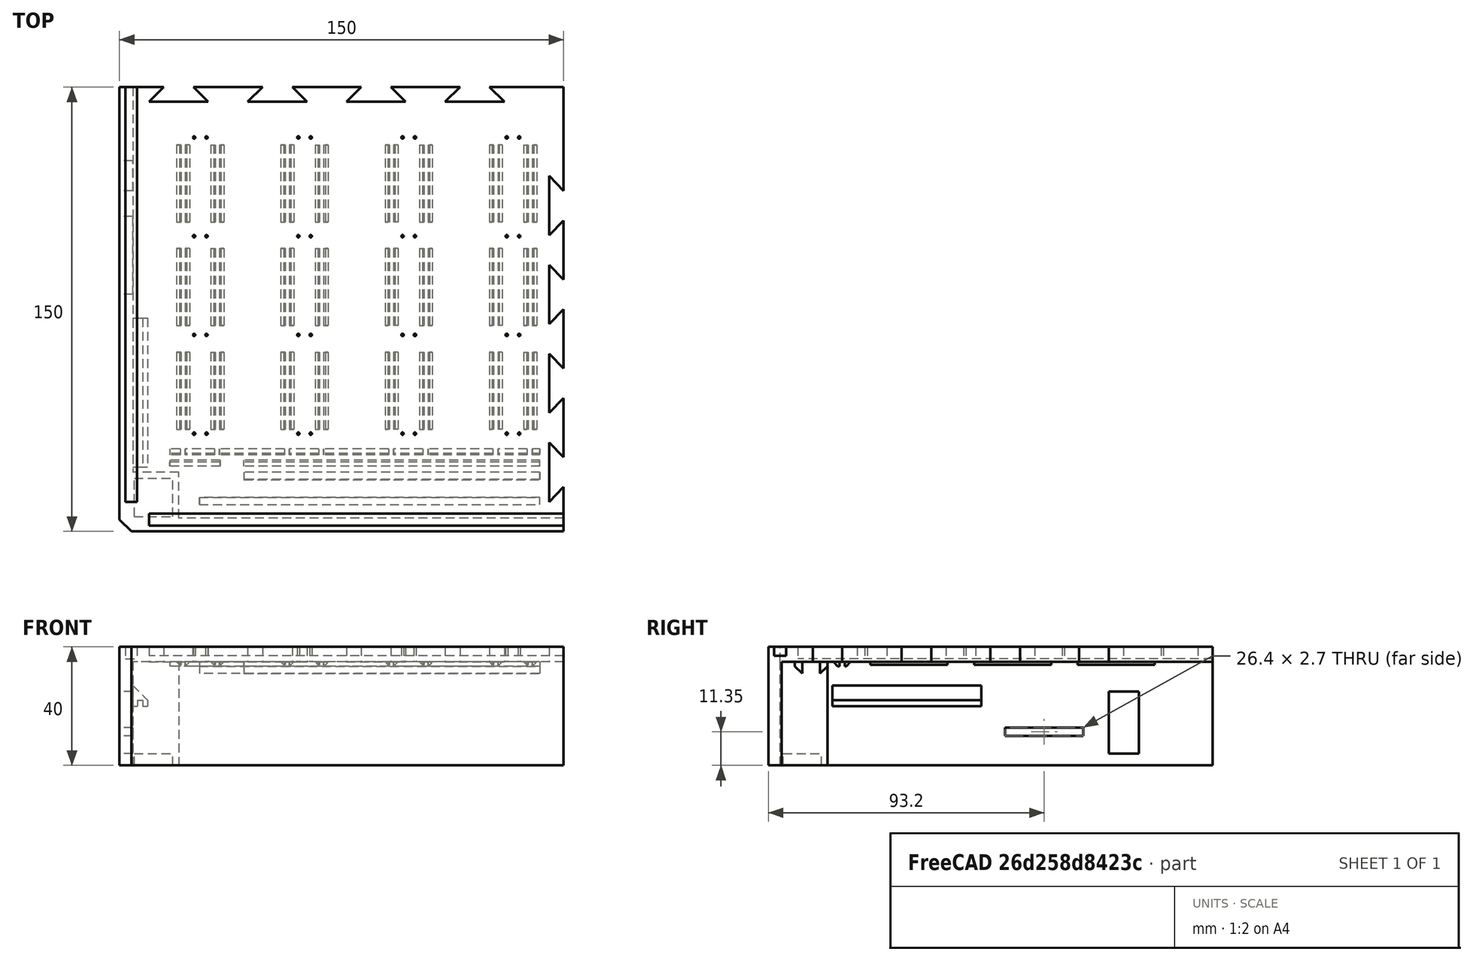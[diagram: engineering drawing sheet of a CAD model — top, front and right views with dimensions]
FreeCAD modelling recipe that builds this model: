
FCSTD DOCUMENT  (FreeCAD 0.19R24267 +148 (Git))
Label: LED CUBE_LIJEVI DONJI DIO ISPRAVAK
License: All rights reserved
LicenseURL: http://en.wikipedia.org/wiki/All_rights_reserved
objects: Sketcher::SketchObject×18, PartDesign::Pocket×9, PartDesign::Pad×8, PartDesign::Chamfer×6, PartDesign::LinearPattern×4, PartDesign::Hole×1, PartDesign::Body×1
note: 71 computed .brp shape members not serialized (recipe doc carries the construction recipe); baked Part::Feature solids carry a one-line shape summary decoded from their .brp

FEATURE [Sketcher::SketchObject] Sketch
  FullyConstrained = true
  MapMode = 5
  Support = -> [XY_Plane]
  sketch-geometry (4):
    g0: LineSegment StartX=0 StartY=0 StartZ=0 EndX=150 EndY=0 EndZ=0
    g1: LineSegment StartX=150 StartY=0 StartZ=0 EndX=150 EndY=150 EndZ=0
    g2: LineSegment StartX=150 StartY=150 StartZ=0 EndX=0 EndY=150 EndZ=0
    g3: LineSegment StartX=0 StartY=150 StartZ=0 EndX=0 EndY=0 EndZ=0
  constraints (11):
    c: Coincident(g0,g1)
    c: Coincident(g1,g2)
    c: Coincident(g2,g3)
    c: Coincident(g3,g0)
    c: Horizontal(g0)
    c: Horizontal(g2)
    c: Vertical(g1)
    c: Vertical(g3)
    c: Coincident(g0,g-1)
    c: DistanceX(g2,g2) = 150
    c: DistanceY(g1,g1) = 150
FEATURE [PartDesign::Pad] Pad
  Direction = (1,1,1)
  Length = 5
  Length2 = 100
  Profile = -> Sketch
  Type = 0
FEATURE [Sketcher::SketchObject] Sketch001
  FullyConstrained = true
  MapMode = 5
  Placement = pos=(0,0,5) rot=(0,0,1;0rad)
  Support = -> [Pad]
  sketch-geometry (6):
    g0: LineSegment StartX=0 StartY=0 StartZ=0 EndX=150 EndY=0 EndZ=0
    g1: LineSegment StartX=150 StartY=0 StartZ=0 EndX=150 EndY=15 EndZ=0
    g2: LineSegment StartX=150 StartY=15 StartZ=0 EndX=150 EndY=25 EndZ=0
    g3: LineSegment StartX=150 StartY=15 StartZ=0 EndX=145.101 EndY=10 EndZ=0
    g4: LineSegment StartX=145.101 StartY=10 StartZ=0 EndX=145.101 EndY=30 EndZ=0
    g5: LineSegment StartX=150 StartY=25 StartZ=0 EndX=145.101 EndY=30 EndZ=0
  constraints (17):
    c: Coincident(g0,g-1)
    c: Horizontal(g0)
    c: DistanceX(g0,g0) = 150
    c: Coincident(g1,g0)
    c: Vertical(g1)
    c: DistanceY(g1,g1) = 15
    c: Coincident(g2,g1)
    c: Vertical(g2)
    c: DistanceY(g2,g2) = 10
    c: Coincident(g3,g2)
    c: Distance(g3) = 7
    c: Coincident(g4,g3)
    c: Vertical(g4)
    c: DistanceY(g4,g4) = 20
    c: Coincident(g5,g2)
    c: Coincident(g5,g4)
    c: Distance(g5) = 7
FEATURE [PartDesign::Pocket] Pocket
  BaseFeature = -> Pad
  Length = 8
  Length2 = 100
  Profile = -> Sketch001
  Type = 0
FEATURE [PartDesign::LinearPattern] LinearPattern
  BaseFeature = -> Pocket
  Direction = -> Y_Axis
  Length = 90
  Occurrences = 4
  Originals = -> [Pocket]
FEATURE [Sketcher::SketchObject] Sketch002
  FullyConstrained = true
  MapMode = 5
  Placement = pos=(0,0,5) rot=(0,0,1;0rad)
  Support = -> [LinearPattern]
  sketch-geometry (6):
    g0: LineSegment StartX=0 StartY=0 StartZ=0 EndX=0 EndY=150 EndZ=0
    g1: LineSegment StartX=0 StartY=150 StartZ=0 EndX=15 EndY=150 EndZ=0
    g2: LineSegment StartX=15 StartY=150 StartZ=0 EndX=25 EndY=150 EndZ=0
    g3: LineSegment StartX=15 StartY=150 StartZ=0 EndX=10 EndY=145.101 EndZ=0
    g4: LineSegment StartX=10 StartY=145.101 StartZ=0 EndX=30 EndY=145.101 EndZ=0
    g5: LineSegment StartX=25 StartY=150 StartZ=0 EndX=30 EndY=145.101 EndZ=0
  constraints (17):
    c: Coincident(g0,g-1)
    c: PointOnObject(g0,g-2)
    c: DistanceY(g0,g0) = 150
    c: Coincident(g1,g0)
    c: Horizontal(g1)
    c: DistanceX(g1,g1) = 15
    c: Coincident(g2,g1)
    c: Horizontal(g2)
    c: DistanceX(g2,g2) = 10
    c: Coincident(g3,g2)
    c: Distance(g3) = 7
    c: Coincident(g4,g3)
    c: Horizontal(g4)
    c: DistanceX(g4,g4) = 20
    c: Coincident(g5,g2)
    c: Coincident(g5,g4)
    c: Distance(g5) = 7
FEATURE [PartDesign::Pocket] Pocket001
  BaseFeature = -> LinearPattern
  Length = 8
  Length2 = 100
  Profile = -> Sketch002
  Type = 0
FEATURE [PartDesign::LinearPattern] LinearPattern001
  BaseFeature = -> Pocket001
  Direction = -> X_Axis
  Length = 100
  Occurrences = 4
  Originals = -> [Pocket001]
FEATURE [Sketcher::SketchObject] Sketch003
  FullyConstrained = true
  MapMode = 5
  Placement = pos=(0,0,0) rot=(1,0,0;3.14159rad)
  Support = -> [LinearPattern001]
  sketch-geometry (8):
    g0: LineSegment StartX=0 StartY=0 StartZ=0 EndX=150 EndY=0 EndZ=0
    g1: LineSegment StartX=150 StartY=0 StartZ=0 EndX=150 EndY=-4.5 EndZ=0
    g2: LineSegment StartX=150 StartY=-4.5 StartZ=0 EndX=20 EndY=-4.5 EndZ=0
    g3: LineSegment StartX=0 StartY=0 StartZ=0 EndX=0 EndY=-150 EndZ=0
    g4: LineSegment StartX=0 StartY=-150 StartZ=0 EndX=4.5 EndY=-150 EndZ=0
    g5: LineSegment StartX=4.5 StartY=-150 StartZ=0 EndX=4.5 EndY=-20 EndZ=0
    g6: LineSegment StartX=20 StartY=-4.5 StartZ=0 EndX=20 EndY=-20 EndZ=0
    g7: LineSegment StartX=20 StartY=-20 StartZ=0 EndX=4.5 EndY=-20 EndZ=0
  constraints (24):
    c: Coincident(g0,g-1)
    c: Horizontal(g0)
    c: DistanceX(g0,g0) = 150
    c: Coincident(g1,g0)
    c: Vertical(g1)
    c: DistanceY(g1,g1) = 4.5
    c: Coincident(g2,g1)
    c: Horizontal(g2)
    c: DistanceX(g2,g2) = 130
    c: Coincident(g3,g0)
    c: PointOnObject(g3,g-2)
    c: DistanceY(g3,g3) = 150
    c: Coincident(g4,g3)
    c: Horizontal(g4)
    c: DistanceX(g4,g4) = 4.5
    c: Coincident(g5,g4)
    c: Vertical(g5)
    c: DistanceY(g5,g5) = 130
    c: Coincident(g6,g2)
    c: Vertical(g6)
    c: DistanceY(g6,g6) = 15.5
    c: Coincident(g7,g6)
    c: Horizontal(g7)
    c: DistanceX(g7,g7) = 15.5
FEATURE [PartDesign::Pad] Pad001
  BaseFeature = -> LinearPattern001
  Direction = (1,1,1)
  Length = 35
  Length2 = 100
  Profile = -> Sketch003
  Type = 0
FEATURE [Sketcher::SketchObject] Sketch004
  FullyConstrained = true
  MapMode = 5
  Placement = pos=(0,0,5) rot=(0,0,1;0rad)
  Support = -> [Pad001]
  sketch-geometry (19):
    g0: LineSegment StartX=0 StartY=0 StartZ=0 EndX=150 EndY=0 EndZ=0
    g1: LineSegment StartX=150 StartY=0 StartZ=0 EndX=150 EndY=50 EndZ=0
    g2: LineSegment StartX=135 StartY=-1e-16 StartZ=0 EndX=135 EndY=33 EndZ=0
    g3: LineSegment StartX=150 StartY=33 StartZ=0 EndX=135 EndY=33 EndZ=0
    g4: Circle CenterX=135 CenterY=33 CenterZ=0 NormalX=0 NormalY=0 NormalZ=1 AngleXU=0 Radius=0.6
    g5: LineSegment StartX=135 StartY=33 StartZ=0 EndX=130.8 EndY=33 EndZ=0
    g6: Circle CenterX=130.8 CenterY=33 CenterZ=0 NormalX=0 NormalY=0 NormalZ=1 AngleXU=0 Radius=0.6
    g7: LineSegment StartX=130.8 StartY=33 StartZ=0 EndX=99.8 EndY=33 EndZ=0
    g8: Circle CenterX=99.8 CenterY=33 CenterZ=0 NormalX=0 NormalY=0 NormalZ=1 AngleXU=0 Radius=0.6
    g9: LineSegment StartX=99.8 StartY=33 StartZ=0 EndX=95.6 EndY=33 EndZ=0
    g10: Circle CenterX=95.6 CenterY=33 CenterZ=0 NormalX=0 NormalY=0 NormalZ=1 AngleXU=0 Radius=0.6
    g11: LineSegment StartX=95.6 StartY=33 StartZ=0 EndX=64.6 EndY=33 EndZ=0
    g12: Circle CenterX=64.6 CenterY=33 CenterZ=0 NormalX=0 NormalY=0 NormalZ=1 AngleXU=0 Radius=0.6
    g13: LineSegment StartX=64.6 StartY=33 StartZ=0 EndX=60.4 EndY=33 EndZ=0
    g14: Circle CenterX=60.4 CenterY=33 CenterZ=0 NormalX=0 NormalY=0 NormalZ=1 AngleXU=0 Radius=0.6
    g15: LineSegment StartX=60.4 StartY=33 StartZ=0 EndX=29.4 EndY=33 EndZ=0
    g16: Circle CenterX=29.4 CenterY=33 CenterZ=0 NormalX=0 NormalY=0 NormalZ=1 AngleXU=0 Radius=0.6
    g17: LineSegment StartX=29.4 StartY=33 StartZ=0 EndX=25.2 EndY=33 EndZ=0
    g18: Circle CenterX=25.2 CenterY=33 CenterZ=0 NormalX=0 NormalY=0 NormalZ=1 AngleXU=0 Radius=0.6
  constraints (50):
    c: Coincident(g0,g-1)
    c: Horizontal(g0)
    c: DistanceX(g0,g0) = 150
    c: Coincident(g1,g0)
    c: Vertical(g1)
    c: DistanceY(g1,g1) = 50
    c: PointOnObject(g2,g0)
    c: Vertical(g2)
    c: PointOnObject(g3,g1)
    c: Coincident(g3,g2)
    c: Horizontal(g3)
    c: DistanceX(g3,g3) = 15
    c: Coincident(g4,g2)
    c: Radius(g4) = 0.6
    c: Coincident(g5,g4)
    c: Horizontal(g5)
    c: DistanceX(g5,g5) = 4.2
    c: Coincident(g6,g5)
    c: Radius(g6) = 0.6
    c: Coincident(g7,g6)
    c: Horizontal(g7)
    c: DistanceX(g7,g7) = 31
    c: Coincident(g8,g7)
    c: Radius(g8) = 0.6
    c: Coincident(g9,g8)
    c: Horizontal(g9)
    c: DistanceX(g9,g9) = 4.2
    c: Coincident(g10,g9)
    c: Radius(g10) = 0.6
    c: Coincident(g11,g10)
    c: Horizontal(g11)
    c: DistanceX(g11,g11) = 31
    c: Coincident(g12,g11)
    c: Radius(g12) = 0.6
    c: Coincident(g13,g12)
    c: Horizontal(g13)
    c: DistanceX(g13,g13) = 4.2
    c: Coincident(g14,g13)
    c: Radius(g14) = 0.6
    c: Coincident(g15,g14)
    c: Horizontal(g15)
    c: DistanceX(g15,g15) = 31
    c: Coincident(g16,g15)
    c: Radius(g16) = 0.6
    c: Coincident(g17,g16)
    c: Horizontal(g17)
    c: DistanceX(g17,g17) = 4.2
    c: Coincident(g18,g17)
    c: Radius(g18) = 0.6
    c: DistanceY(g2,g2) = 33
FEATURE [PartDesign::Hole] Hole
  BaseFeature = -> Pad001
  Depth = 25
  DepthType = 0
  Diameter = 0.8
  DrillForDepth = false
  DrillPoint = 1
  DrillPointAngle = 118
  HoleCutCountersinkAngle = 90
  HoleCutCustomValues = false
  HoleCutDepth = 0
  HoleCutDiameter = 6.1
  HoleCutType = 0
  ModelActualThread = false
  Profile = -> Sketch004
  Tapered = false
  TaperedAngle = 90
  ThreadAngle = 0
  ThreadClass = 0
  ThreadCutOffInner = 0
  ThreadCutOffOuter = 0
  ThreadDirection = 0
  ThreadFit = 0
  ThreadPitch = 0
  ThreadSize = 0
  ThreadType = 0
  Threaded = false
FEATURE [PartDesign::LinearPattern] LinearPattern003
  BaseFeature = -> Hole
  Direction = -> Y_Axis
  Length = 100
  Occurrences = 4
  Originals = -> [Hole]
FEATURE [PartDesign::Chamfer] Chamfer
  Angle = 45
  Base = -> LinearPattern003 [Edge1]
  BaseFeature = -> LinearPattern003
  ChamferType = 0
  FlipDirection = false
  Size = 4
  Size2 = 1
  SupportTransform = false
FEATURE [Sketcher::SketchObject] Sketch005
  FullyConstrained = true
  MapMode = 5
  Placement = pos=(0,0,5) rot=(0,0,1;0rad)
  Support = -> [LinearPattern003]
  sketch-geometry (6):
    g0: LineSegment StartX=0 StartY=0 StartZ=0 EndX=0 EndY=150 EndZ=0
    g1: LineSegment StartX=0 StartY=150 StartZ=0 EndX=2 EndY=150 EndZ=0
    g2: LineSegment StartX=2 StartY=150 StartZ=0 EndX=6 EndY=150 EndZ=0
    g3: LineSegment StartX=2 StartY=150 StartZ=0 EndX=2 EndY=10 EndZ=0
    g4: LineSegment StartX=2 StartY=10 StartZ=0 EndX=6 EndY=10 EndZ=0
    g5: LineSegment StartX=6 StartY=10 StartZ=0 EndX=6 EndY=150 EndZ=0
  constraints (18):
    c: Coincident(g0,g-1)
    c: PointOnObject(g0,g-2)
    c: DistanceY(g0,g0) = 150
    c: Coincident(g1,g0)
    c: Horizontal(g1)
    c: DistanceX(g1,g1) = 2
    c: Coincident(g2,g1)
    c: Horizontal(g2)
    c: DistanceX(g2,g2) = 4
    c: Coincident(g3,g2)
    c: Vertical(g3)
    c: DistanceY(g3,g3) = 140
    c: Coincident(g4,g3)
    c: Horizontal(g4)
    c: DistanceX(g4,g4) = 4
    c: Coincident(g5,g4)
    c: Vertical(g5)
    c: DistanceY(g5,g5) = 140
FEATURE [PartDesign::Pocket] Pocket002
  BaseFeature = -> Chamfer
  Length = 4
  Length2 = 100
  Profile = -> Sketch005
  Type = 0
FEATURE [Sketcher::SketchObject] Sketch006
  FullyConstrained = true
  MapMode = 5
  Placement = pos=(0,0,5) rot=(0,0,1;0rad)
  Support = -> [Pocket002]
  sketch-geometry (6):
    g0: LineSegment StartX=0 StartY=0 StartZ=0 EndX=150 EndY=0 EndZ=0
    g1: LineSegment StartX=150 StartY=0 StartZ=0 EndX=150 EndY=2 EndZ=0
    g2: LineSegment StartX=150 StartY=2 StartZ=0 EndX=10 EndY=2 EndZ=0
    g3: LineSegment StartX=150 StartY=2 StartZ=0 EndX=150 EndY=6 EndZ=0
    g4: LineSegment StartX=150 StartY=6 StartZ=0 EndX=10 EndY=6 EndZ=0
    g5: LineSegment StartX=10 StartY=6 StartZ=0 EndX=10 EndY=2 EndZ=0
  constraints (17):
    c: Coincident(g0,g-1)
    c: PointOnObject(g0,g-1)
    c: DistanceX(g0,g0) = 150
    c: Coincident(g1,g0)
    c: Vertical(g1)
    c: DistanceY(g1,g1) = 2
    c: Coincident(g2,g1)
    c: Horizontal(g2)
    c: DistanceX(g2,g2) = 140
    c: Coincident(g3,g2)
    c: Vertical(g3)
    c: DistanceY(g3,g3) = 4
    c: Coincident(g4,g3)
    c: Horizontal(g4)
    c: DistanceX(g4,g4) = 140
    c: Coincident(g5,g4)
    c: Coincident(g5,g2)
FEATURE [PartDesign::Pocket] Pocket003
  BaseFeature = -> Pocket002
  Length = 3
  Length2 = 100
  Profile = -> Sketch006
  Type = 0
FEATURE [Sketcher::SketchObject] Sketch008
  FullyConstrained = true
  MapMode = 5
  Placement = pos=(0,0,-35) rot=(1,0,0;3.14159rad)
  Support = -> [Pocket003]
  sketch-geometry (7):
    g0: LineSegment StartX=0 StartY=0 StartZ=0 EndX=150 EndY=0 EndZ=0
    g1: LineSegment StartX=0 StartY=0 StartZ=0 EndX=0 EndY=-5 EndZ=0
    g2: LineSegment StartX=0 StartY=-5 StartZ=0 EndX=5 EndY=-5 EndZ=0
    g3: LineSegment StartX=5 StartY=-5 StartZ=0 EndX=18 EndY=-5 EndZ=0
    g4: LineSegment StartX=5 StartY=-5 StartZ=0 EndX=5 EndY=-18 EndZ=0
    g5: LineSegment StartX=5 StartY=-18 StartZ=0 EndX=18 EndY=-18 EndZ=0
    g6: LineSegment StartX=18 StartY=-5 StartZ=0 EndX=18 EndY=-18 EndZ=0
  constraints (20):
    c: Coincident(g0,g-1)
    c: PointOnObject(g0,g-1)
    c: DistanceX(g0,g0) = 150
    c: Coincident(g1,g-1)
    c: PointOnObject(g1,g-2)
    c: DistanceY(g1,g1) = 5
    c: Coincident(g2,g1)
    c: Horizontal(g2)
    c: DistanceX(g2,g2) = 5
    c: Coincident(g3,g2)
    c: Horizontal(g3)
    c: DistanceX(g3,g3) = 13
    c: Coincident(g4,g3)
    c: Vertical(g4)
    c: DistanceY(g4,g4) = 13
    c: Coincident(g5,g4)
    c: Horizontal(g5)
    c: DistanceX(g5,g5) = 13
    c: Coincident(g6,g3)
    c: Coincident(g6,g5)
FEATURE [PartDesign::Pocket] Pocket004
  BaseFeature = -> Pocket003
  Length = 4
  Length2 = 100
  Profile = -> Sketch008
  Type = 0
FEATURE [Sketcher::SketchObject] Sketch009
  FullyConstrained = true
  MapMode = 5
  Placement = pos=(0,0,0) rot=(1,0,0;3.14159rad)
  Support = -> [Pocket004]
  sketch-geometry (100):
    g0: LineSegment StartX=0 StartY=0 StartZ=0 EndX=0 EndY=-150 EndZ=0
    g1: LineSegment StartX=0 StartY=0 StartZ=0 EndX=150 EndY=0 EndZ=0
    g2: LineSegment StartX=150 StartY=0 StartZ=0 EndX=150 EndY=-150 EndZ=0
    g3: LineSegment StartX=150 StartY=-150 StartZ=0 EndX=135 EndY=-150 EndZ=0
    g4: LineSegment StartX=135 StartY=-150 StartZ=0 EndX=135 EndY=-133 EndZ=0
    g5: LineSegment StartX=135 StartY=-133 StartZ=0 EndX=136.5 EndY=-133 EndZ=0
    g6: LineSegment StartX=136.5 StartY=-133 StartZ=0 EndX=136.5 EndY=-130.5 EndZ=0
    g7: LineSegment StartX=136.5 StartY=-130.5 StartZ=0 EndX=138 EndY=-130.5 EndZ=0
    g8: LineSegment StartX=136.5 StartY=-130.5 StartZ=0 EndX=136.5 EndY=-104.5 EndZ=0
    g9: LineSegment StartX=138 StartY=-130.5 StartZ=0 EndX=138 EndY=-104.5 EndZ=0
    g10: LineSegment StartX=138 StartY=-130.5 StartZ=0 EndX=139.4 EndY=-130.5 EndZ=0
    g11: LineSegment StartX=139.4 StartY=-130.5 StartZ=0 EndX=140.9 EndY=-130.5 EndZ=0
    g12: LineSegment StartX=139.4 StartY=-130.5 StartZ=0 EndX=139.4 EndY=-104.5 EndZ=0
    g13: LineSegment StartX=140.9 StartY=-130.5 StartZ=0 EndX=140.9 EndY=-104.5 EndZ=0
    g14: LineSegment StartX=138 StartY=-104.5 StartZ=0 EndX=136.5 EndY=-104.5 EndZ=0
    g15: LineSegment StartX=139.4 StartY=-104.5 StartZ=0 EndX=140.9 EndY=-104.5 EndZ=0
    g16: LineSegment StartX=135 StartY=-133 StartZ=0 EndX=130.8 EndY=-133 EndZ=0
    g17: LineSegment StartX=130.8 StartY=-133 StartZ=0 EndX=130.8 EndY=-130.5 EndZ=0
    g18: LineSegment StartX=130.8 StartY=-130.5 StartZ=0 EndX=129.3 EndY=-130.5 EndZ=0
    g19: LineSegment StartX=129.3 StartY=-130.5 StartZ=0 EndX=127.8 EndY=-130.5 EndZ=0
    g20: LineSegment StartX=129.3 StartY=-130.5 StartZ=0 EndX=129.3 EndY=-104.5 EndZ=0
    g21: LineSegment StartX=127.8 StartY=-130.5 StartZ=0 EndX=127.8 EndY=-104.5 EndZ=0
    g22: LineSegment StartX=127.8 StartY=-130.5 StartZ=0 EndX=126.4 EndY=-130.5 EndZ=0
    g23: LineSegment StartX=126.4 StartY=-130.5 StartZ=0 EndX=126.4 EndY=-104.5 EndZ=0
    g24: LineSegment StartX=126.4 StartY=-130.5 StartZ=0 EndX=124.9 EndY=-130.5 EndZ=0
    g25: LineSegment StartX=124.9 StartY=-130.5 StartZ=0 EndX=124.9 EndY=-104.5 EndZ=0
    g26: LineSegment StartX=126.4 StartY=-104.5 StartZ=0 EndX=124.9 EndY=-104.5 EndZ=0
    g27: LineSegment StartX=129.3 StartY=-104.5 StartZ=0 EndX=127.8 EndY=-104.5 EndZ=0
    g28: LineSegment StartX=130.8 StartY=-133 StartZ=0 EndX=99.8 EndY=-133 EndZ=0
    g29: LineSegment StartX=99.8 StartY=-133 StartZ=0 EndX=99.8 EndY=-130.5 EndZ=0
    g30: LineSegment StartX=99.8 StartY=-130.5 StartZ=0 EndX=101.3 EndY=-130.5 EndZ=0
    g31: LineSegment StartX=101.3 StartY=-130.5 StartZ=0 EndX=102.8 EndY=-130.5 EndZ=0
    g32: LineSegment StartX=101.3 StartY=-130.5 StartZ=0 EndX=101.3 EndY=-104.5 EndZ=0
    g33: LineSegment StartX=102.8 StartY=-130.5 StartZ=0 EndX=102.8 EndY=-104.5 EndZ=0
    g34: LineSegment StartX=102.8 StartY=-130.5 StartZ=0 EndX=104.2 EndY=-130.5 EndZ=0
    g35: LineSegment StartX=104.2 StartY=-130.5 StartZ=0 EndX=105.7 EndY=-130.5 EndZ=0
    g36: LineSegment StartX=104.2 StartY=-130.5 StartZ=0 EndX=104.2 EndY=-104.5 EndZ=0
    g37: LineSegment StartX=105.7 StartY=-130.5 StartZ=0 EndX=105.7 EndY=-104.5 EndZ=0
    g38: LineSegment StartX=101.3 StartY=-104.5 StartZ=0 EndX=102.8 EndY=-104.5 EndZ=0
    g39: LineSegment StartX=104.2 StartY=-104.5 StartZ=0 EndX=105.7 EndY=-104.5 EndZ=0
    g40: LineSegment StartX=99.8 StartY=-133 StartZ=0 EndX=95.6 EndY=-133 EndZ=0
    g41: LineSegment StartX=95.6 StartY=-133 StartZ=0 EndX=95.6 EndY=-130.5 EndZ=0
    g42: LineSegment StartX=95.6 StartY=-130.5 StartZ=0 EndX=94.1 EndY=-130.5 EndZ=0
    g43: LineSegment StartX=94.1 StartY=-130.5 StartZ=0 EndX=92.6 EndY=-130.5 EndZ=0
    g44: LineSegment StartX=94.1 StartY=-130.5 StartZ=0 EndX=94.1 EndY=-104.5 EndZ=0
    g45: LineSegment StartX=92.6 StartY=-130.5 StartZ=0 EndX=92.6 EndY=-104.5 EndZ=0
    g46: LineSegment StartX=92.6 StartY=-130.5 StartZ=0 EndX=91.2 EndY=-130.5 EndZ=0
    g47: LineSegment StartX=91.2 StartY=-130.5 StartZ=0 EndX=89.7 EndY=-130.5 EndZ=0
    g48: LineSegment StartX=91.2 StartY=-130.5 StartZ=0 EndX=91.2 EndY=-104.5 EndZ=0
    g49: LineSegment StartX=89.7 StartY=-130.5 StartZ=0 EndX=89.7 EndY=-104.5 EndZ=0
    g50: LineSegment StartX=91.2 StartY=-104.5 StartZ=0 EndX=89.7 EndY=-104.5 EndZ=0
    g51: LineSegment StartX=94.1 StartY=-104.5 StartZ=0 EndX=92.6 EndY=-104.5 EndZ=0
    g52: LineSegment StartX=95.6 StartY=-133 StartZ=0 EndX=64.6 EndY=-133 EndZ=0
    g53: LineSegment StartX=64.6 StartY=-133 StartZ=0 EndX=64.6 EndY=-130.5 EndZ=0
    g54: LineSegment StartX=64.6 StartY=-130.5 StartZ=0 EndX=66.1 EndY=-130.5 EndZ=0
    g55: LineSegment StartX=66.1 StartY=-130.5 StartZ=0 EndX=67.6 EndY=-130.5 EndZ=0
    g56: LineSegment StartX=67.6 StartY=-130.5 StartZ=0 EndX=67.6 EndY=-104.5 EndZ=0
    g57: LineSegment StartX=66.1 StartY=-130.5 StartZ=0 EndX=66.1 EndY=-104.5 EndZ=0
    g58: LineSegment StartX=67.6 StartY=-130.5 StartZ=0 EndX=69 EndY=-130.5 EndZ=0
    g59: LineSegment StartX=69 StartY=-130.5 StartZ=0 EndX=70.5 EndY=-130.5 EndZ=0
    g60: LineSegment StartX=69 StartY=-130.5 StartZ=0 EndX=69 EndY=-104.5 EndZ=0
    g61: LineSegment StartX=70.5 StartY=-130.5 StartZ=0 EndX=70.5 EndY=-104.5 EndZ=0
    g62: LineSegment StartX=66.1 StartY=-104.5 StartZ=0 EndX=67.6 EndY=-104.5 EndZ=0
    g63: LineSegment StartX=69 StartY=-104.5 StartZ=0 EndX=70.5 EndY=-104.5 EndZ=0
    g64: LineSegment StartX=64.6 StartY=-133 StartZ=0 EndX=60.4 EndY=-133 EndZ=0
    g65: LineSegment StartX=60.4 StartY=-133 StartZ=0 EndX=60.4 EndY=-130.5 EndZ=0
    g66: LineSegment StartX=60.4 StartY=-130.5 StartZ=0 EndX=58.9 EndY=-130.5 EndZ=0
    g67: LineSegment StartX=58.9 StartY=-130.5 StartZ=0 EndX=57.4 EndY=-130.5 EndZ=0
    g68: LineSegment StartX=58.9 StartY=-130.5 StartZ=0 EndX=58.9 EndY=-104.5 EndZ=0
    g69: LineSegment StartX=57.4 StartY=-130.5 StartZ=0 EndX=57.4 EndY=-104.5 EndZ=0
    g70: LineSegment StartX=57.4 StartY=-130.5 StartZ=0 EndX=56 EndY=-130.5 EndZ=0
    g71: LineSegment StartX=56 StartY=-130.5 StartZ=0 EndX=54.5 EndY=-130.5 EndZ=0
    g72: LineSegment StartX=56 StartY=-130.5 StartZ=0 EndX=56 EndY=-104.5 EndZ=0
    g73: LineSegment StartX=54.5 StartY=-130.5 StartZ=0 EndX=54.5 EndY=-104.5 EndZ=0
    g74: LineSegment StartX=54.5 StartY=-104.5 StartZ=0 EndX=56 EndY=-104.5 EndZ=0
    g75: LineSegment StartX=57.4 StartY=-104.5 StartZ=0 EndX=58.9 EndY=-104.5 EndZ=0
    g76: LineSegment StartX=60.4 StartY=-133 StartZ=0 EndX=29.4 EndY=-133 EndZ=0
    g77: LineSegment StartX=29.4 StartY=-133 StartZ=0 EndX=29.4 EndY=-130.5 EndZ=0
    g78: LineSegment StartX=29.4 StartY=-130.5 StartZ=0 EndX=30.9 EndY=-130.5 EndZ=0
    g79: LineSegment StartX=30.9 StartY=-130.5 StartZ=0 EndX=32.4 EndY=-130.5 EndZ=0
    g80: LineSegment StartX=30.9 StartY=-130.5 StartZ=0 EndX=30.9 EndY=-104.5 EndZ=0
    g81: LineSegment StartX=32.4 StartY=-130.5 StartZ=0 EndX=32.4 EndY=-104.5 EndZ=0
    g82: LineSegment StartX=29.4 StartY=-133 StartZ=0 EndX=25.2 EndY=-133 EndZ=0
    g83: LineSegment StartX=25.2 StartY=-133 StartZ=0 EndX=25.2 EndY=-130.5 EndZ=0
    g84: LineSegment StartX=25.2 StartY=-130.5 StartZ=0 EndX=23.7 EndY=-130.5 EndZ=0
    g85: LineSegment StartX=23.7 StartY=-130.5 StartZ=0 EndX=22.2 EndY=-130.5 EndZ=0
    g86: LineSegment StartX=23.7 StartY=-130.5 StartZ=0 EndX=23.7 EndY=-104.5 EndZ=0
    g87: LineSegment StartX=22.2 StartY=-130.5 StartZ=0 EndX=22.2 EndY=-104.5 EndZ=0
    g88: LineSegment StartX=22.2 StartY=-130.5 StartZ=0 EndX=20.8 EndY=-130.5 EndZ=0
    g89: LineSegment StartX=20.8 StartY=-130.5 StartZ=0 EndX=19.3 EndY=-130.5 EndZ=0
    g90: LineSegment StartX=20.8 StartY=-130.5 StartZ=0 EndX=20.8 EndY=-104.5 EndZ=0
    g91: LineSegment StartX=19.3 StartY=-130.5 StartZ=0 EndX=19.3 EndY=-104.5 EndZ=0
    g92: LineSegment StartX=19.3 StartY=-104.5 StartZ=0 EndX=20.8 EndY=-104.5 EndZ=0
    g93: LineSegment StartX=22.2 StartY=-104.5 StartZ=0 EndX=23.7 EndY=-104.5 EndZ=0
    g94: LineSegment StartX=32.4 StartY=-130.5 StartZ=0 EndX=33.8 EndY=-130.5 EndZ=0
    g95: LineSegment StartX=33.8 StartY=-130.5 StartZ=0 EndX=35.3 EndY=-130.5 EndZ=0
    g96: LineSegment StartX=33.8 StartY=-130.5 StartZ=0 EndX=33.8 EndY=-104.5 EndZ=0
    g97: LineSegment StartX=35.3 StartY=-130.5 StartZ=0 EndX=35.3 EndY=-104.5 EndZ=0
    g98: LineSegment StartX=30.9 StartY=-104.5 StartZ=0 EndX=32.4 EndY=-104.5 EndZ=0
    g99: LineSegment StartX=33.8 StartY=-104.5 StartZ=0 EndX=35.3 EndY=-104.5 EndZ=0
  constraints (284):
    c: Coincident(g0,g-1)
    c: PointOnObject(g0,g-2)
    c: DistanceY(g0,g0) = 150
    c: Coincident(g1,g-1)
    c: PointOnObject(g1,g-1)
    c: DistanceX(g1,g1) = 150
    c: Coincident(g2,g1)
    c: Vertical(g2)
    c: DistanceY(g2,g2) = 150
    c: Coincident(g3,g2)
    c: Horizontal(g3)
    c: DistanceX(g3,g3) = 15
    c: Coincident(g4,g3)
    c: Vertical(g4)
    c: DistanceY(g4,g4) = 17
    c: Coincident(g5,g4)
    c: Horizontal(g5)
    c: DistanceX(g5,g5) = 1.5
    c: Coincident(g6,g5)
    c: Vertical(g6)
    c: DistanceY(g6,g6) = 2.5
    c: Coincident(g7,g6)
    c: Horizontal(g7)
    c: DistanceX(g7,g7) = 1.5
    c: Coincident(g8,g7)
    c: Vertical(g8)
    c: DistanceY(g8,g8) = 26
    c: Coincident(g9,g7)
    c: Vertical(g9)
    c: DistanceY(g9,g9) = 26
    c: Coincident(g10,g7)
    c: Horizontal(g10)
    c: DistanceX(g10,g10) = 1.4
    c: Coincident(g11,g10)
    c: Horizontal(g11)
    c: DistanceX(g11,g11) = 1.5
    c: Coincident(g12,g11)
    c: Vertical(g12)
    c: DistanceY(g12,g12) = 26
    c: Coincident(g13,g11)
    c: Vertical(g13)
    c: DistanceY(g13,g13) = 26
    c: Coincident(g14,g9)
    c: Coincident(g14,g8)
    c: Coincident(g15,g12)
    c: Coincident(g15,g13)
    c: Coincident(g16,g4)
    c: Horizontal(g16)
    c: DistanceX(g16,g16) = 4.2
    c: Coincident(g17,g16)
    c: Vertical(g17)
    c: DistanceY(g17,g17) = 2.5
    c: Coincident(g18,g17)
    c: Horizontal(g18)
    c: DistanceX(g18,g18) = 1.5
    c: Coincident(g19,g18)
    c: Horizontal(g19)
    c: DistanceX(g19,g19) = 1.5
    c: Coincident(g20,g19)
    c: Vertical(g20)
    c: DistanceY(g20,g20) = 26
    c: Coincident(g21,g19)
    c: Vertical(g21)
    c: DistanceY(g21,g21) = 26
    c: Coincident(g22,g19)
    c: Horizontal(g22)
    c: DistanceX(g22,g22) = 1.4
    c: Coincident(g23,g22)
    c: Vertical(g23)
    c: DistanceY(g23,g23) = 26
    c: Coincident(g24,g23)
    c: Horizontal(g24)
    c: DistanceX(g24,g24) = 1.5
    c: Coincident(g25,g24)
    c: Vertical(g25)
    c: DistanceY(g25,g25) = 26
    c: Coincident(g26,g23)
    c: Coincident(g26,g25)
    c: Coincident(g27,g20)
    c: Coincident(g27,g21)
    c: Coincident(g28,g16)
    c: Horizontal(g28)
    c: DistanceX(g28,g28) = 31
    c: Coincident(g29,g28)
    c: Vertical(g29)
    c: DistanceY(g29,g29) = 2.5
    c: Coincident(g30,g29)
    c: Horizontal(g30)
    c: DistanceX(g30,g30) = 1.5
    c: Coincident(g31,g30)
    c: Horizontal(g31)
    c: DistanceX(g31,g31) = 1.5
    c: Coincident(g32,g31)
    c: Vertical(g32)
    c: DistanceY(g32,g32) = 26
    c: Coincident(g33,g31)
    c: Vertical(g33)
    c: DistanceY(g33,g33) = 26
    c: Coincident(g34,g31)
    c: Horizontal(g34)
    c: DistanceX(g34,g34) = 1.4
    c: Coincident(g35,g34)
    c: Horizontal(g35)
    c: DistanceX(g35,g35) = 1.5
    c: Coincident(g36,g35)
    c: Vertical(g36)
    c: DistanceY(g36,g36) = 26
    c: Coincident(g37,g35)
    c: Vertical(g37)
    c: DistanceY(g37,g37) = 26
    c: Coincident(g38,g32)
    c: Coincident(g38,g33)
    c: Coincident(g39,g36)
    c: Coincident(g39,g37)
    c: Coincident(g40,g28)
    c: Horizontal(g40)
    c: DistanceX(g40,g40) = 4.2
    c: Coincident(g41,g40)
    c: Vertical(g41)
    c: DistanceY(g41,g41) = 2.5
    c: Coincident(g42,g41)
    c: Horizontal(g42)
    c: DistanceX(g42,g42) = 1.5
    c: Coincident(g43,g42)
    c: Horizontal(g43)
    c: DistanceX(g43,g43) = 1.5
    c: Coincident(g44,g43)
    c: Vertical(g44)
    c: DistanceY(g44,g44) = 26
    c: Coincident(g45,g43)
    c: Vertical(g45)
    c: DistanceY(g45,g45) = 26
    c: Coincident(g46,g43)
    c: Horizontal(g46)
    c: DistanceX(g46,g46) = 1.4
    c: Coincident(g47,g46)
    c: Horizontal(g47)
    c: DistanceX(g47,g47) = 1.5
    c: Coincident(g48,g47)
    c: Vertical(g48)
    c: DistanceY(g48,g48) = 26
    c: Coincident(g49,g47)
    c: Vertical(g49)
    c: DistanceY(g49,g49) = 26
    c: Coincident(g50,g48)
    c: Coincident(g50,g49)
    c: Coincident(g51,g44)
    c: Coincident(g51,g45)
    c: Coincident(g52,g40)
    c: Horizontal(g52)
    c: DistanceX(g52,g52) = 31
    c: Coincident(g53,g52)
    c: Vertical(g53)
    c: DistanceY(g53,g53) = 2.5
    c: Coincident(g54,g53)
    c: Horizontal(g54)
    c: DistanceX(g54,g54) = 1.5
    c: Coincident(g55,g54)
    c: Horizontal(g55)
    c: DistanceX(g55,g55) = 1.5
    c: Coincident(g56,g55)
    c: Vertical(g56)
    c: DistanceY(g56,g56) = 26
    c: Coincident(g57,g55)
    c: Vertical(g57)
    c: DistanceY(g57,g57) = 26
    c: Coincident(g58,g55)
    c: Horizontal(g58)
    c: DistanceX(g58,g58) = 1.4
    c: Coincident(g59,g58)
    c: Horizontal(g59)
    c: DistanceX(g59,g59) = 1.5
    c: Coincident(g60,g59)
    c: Vertical(g60)
    c: DistanceY(g60,g60) = 26
    c: Coincident(g61,g59)
    c: Vertical(g61)
    c: DistanceY(g61,g61) = 26
    c: Coincident(g62,g57)
    c: Coincident(g62,g56)
    c: Coincident(g63,g60)
    c: Coincident(g63,g61)
    c: Coincident(g64,g52)
    c: Horizontal(g64)
    c: DistanceX(g64,g64) = 4.2
    c: Coincident(g65,g64)
    c: Vertical(g65)
    c: DistanceY(g65,g65) = 2.5
    c: Coincident(g66,g65)
    c: Horizontal(g66)
    c: DistanceX(g66,g66) = 1.5
    c: Coincident(g67,g66)
    c: Horizontal(g67)
    c: DistanceX(g67,g67) = 1.5
    c: Coincident(g68,g67)
    c: Vertical(g68)
    c: DistanceY(g68,g68) = 26
    c: Coincident(g69,g67)
    c: Vertical(g69)
    c: DistanceY(g69,g69) = 26
    c: Coincident(g70,g67)
    c: Horizontal(g70)
    c: DistanceX(g70,g70) = 1.4
    c: Coincident(g71,g70)
    c: Horizontal(g71)
    c: DistanceX(g71,g71) = 1.5
    c: Coincident(g72,g71)
    c: Vertical(g72)
    c: DistanceY(g72,g72) = 26
    c: Coincident(g73,g71)
    c: Vertical(g73)
    c: DistanceY(g73,g73) = 26
    c: Coincident(g74,g73)
    c: Coincident(g74,g72)
    c: Coincident(g75,g69)
    c: Coincident(g75,g68)
    c: Coincident(g76,g64)
    c: Horizontal(g76)
    c: DistanceX(g76,g76) = 31
    c: Coincident(g77,g76)
    c: Vertical(g77)
    c: DistanceY(g77,g77) = 2.5
    c: Coincident(g78,g77)
    c: Horizontal(g78)
    c: DistanceX(g78,g78) = 1.5
    c: Coincident(g79,g78)
    c: Horizontal(g79)
    c: DistanceX(g79,g79) = 1.5
    c: Coincident(g80,g79)
    c: Vertical(g80)
    c: DistanceY(g80,g80) = 26
    c: Coincident(g81,g79)
    c: Vertical(g81)
    c: DistanceY(g81,g81) = 26
    c: Coincident(g82,g76)
    c: Horizontal(g82)
    c: DistanceX(g82,g82) = 4.2
    c: Coincident(g83,g82)
    c: Vertical(g83)
    c: DistanceY(g83,g83) = 2.5
    c: Coincident(g84,g83)
    c: Horizontal(g84)
    c: DistanceX(g84,g84) = 1.5
    c: Coincident(g85,g84)
    c: Horizontal(g85)
    c: DistanceX(g85,g85) = 1.5
    c: Coincident(g86,g85)
    c: Vertical(g86)
    c: DistanceY(g86,g86) = 26
    c: Coincident(g87,g85)
    c: Vertical(g87)
    c: DistanceY(g87,g87) = 26
    c: Coincident(g88,g85)
    c: Horizontal(g88)
    c: DistanceX(g88,g88) = 1.4
    c: Coincident(g89,g88)
    c: Horizontal(g89)
    c: DistanceX(g89,g89) = 1.5
    c: Coincident(g90,g89)
    c: Vertical(g90)
    c: DistanceY(g90,g90) = 26
    c: Coincident(g91,g89)
    c: Vertical(g91)
    c: DistanceY(g91,g91) = 26
    c: Coincident(g92,g91)
    c: Coincident(g92,g90)
    c: Coincident(g93,g87)
    c: Coincident(g93,g86)
    c: Coincident(g94,g79)
    c: Horizontal(g94)
    c: DistanceX(g94,g94) = 1.4
    c: Coincident(g95,g94)
    c: Horizontal(g95)
    c: DistanceX(g95,g95) = 1.5
    c: Coincident(g96,g95)
    c: Vertical(g96)
    c: DistanceY(g96,g96) = 26
    c: Coincident(g97,g95)
    c: Vertical(g97)
    c: DistanceY(g97,g97) = 26
    c: Coincident(g98,g80)
    c: Coincident(g98,g81)
    c: Coincident(g99,g96)
    c: Coincident(g99,g97)
FEATURE [PartDesign::Pad] Pad002
  BaseFeature = -> Pocket004
  Direction = (1,1,1)
  Length = 1
  Length2 = 100
  Profile = -> Sketch009
  Type = 0
FEATURE [PartDesign::LinearPattern] LinearPattern004
  BaseFeature = -> Pad002
  Direction = -> Y_Axis
  Length = 70
  Occurrences = 3
  Originals = -> [Pad002]
  Reversed = true
FEATURE [PartDesign::Chamfer] Chamfer001
  Angle = 45
  Base = -> LinearPattern004 [Edge843,Edge830,Edge824,Edge818,Edge811,Edge798,Edge792,Edge786,Edge779,Edge766,Edge760,Edge754,Edge715,Edge702,Edge696,Edge690,Edge683,Edge670,Edge664,Edge658,Edge587,Edge574,Edge568,Edge562,Edge650,Edge638,Edge635,Edge624,Edge618,Edge606,Edge603,Edge592,Edge522,Edge510,Edge507,Edge496]
  BaseFeature = -> LinearPattern004
  ChamferType = 0
  FlipDirection = false
  Size = 0.99
  Size2 = 1
  SupportTransform = false
FEATURE [Sketcher::SketchObject] Sketch010
  FullyConstrained = true
  MapMode = 5
  Placement = pos=(0,0,0) rot=(1,0,0;3.14159rad)
  Support = -> [Chamfer001]
  sketch-geometry (12):
    g0: LineSegment StartX=0 StartY=0 StartZ=0 EndX=150 EndY=0 EndZ=0
    g1: LineSegment StartX=150 StartY=0 StartZ=0 EndX=150 EndY=-22 EndZ=0
    g2: LineSegment StartX=150 StartY=-22 StartZ=0 EndX=142 EndY=-22 EndZ=0
    g3: LineSegment StartX=142 StartY=-22 StartZ=0 EndX=17 EndY=-22 EndZ=0
    g4: LineSegment StartX=142 StartY=-22 StartZ=0 EndX=142 EndY=-24 EndZ=0
    g5: LineSegment StartX=142 StartY=-24 StartZ=0 EndX=17 EndY=-24 EndZ=0
    g6: LineSegment StartX=142 StartY=-24 StartZ=0 EndX=142 EndY=-25.8 EndZ=0
    g7: LineSegment StartX=142 StartY=-25.8 StartZ=0 EndX=142 EndY=-27.8 EndZ=0
    g8: LineSegment StartX=142 StartY=-25.8 StartZ=0 EndX=17 EndY=-25.8 EndZ=0
    g9: LineSegment StartX=142 StartY=-27.8 StartZ=0 EndX=17 EndY=-27.8 EndZ=0
    g10: LineSegment StartX=17 StartY=-22 StartZ=0 EndX=17 EndY=-24 EndZ=0
    g11: LineSegment StartX=17 StartY=-25.8 StartZ=0 EndX=17 EndY=-27.8 EndZ=0
  constraints (34):
    c: Coincident(g0,g-1)
    c: PointOnObject(g0,g-1)
    c: DistanceX(g0,g0) = 150
    c: Coincident(g1,g0)
    c: Vertical(g1)
    c: DistanceY(g1,g1) = 22
    c: Coincident(g2,g1)
    c: Horizontal(g2)
    c: DistanceX(g2,g2) = 8
    c: Coincident(g3,g2)
    c: Horizontal(g3)
    c: DistanceX(g3,g3) = 125
    c: Coincident(g4,g3)
    c: Vertical(g4)
    c: DistanceY(g4,g4) = 2
    c: Coincident(g5,g4)
    c: Horizontal(g5)
    c: DistanceX(g5,g5) = 125
    c: Coincident(g6,g4)
    c: Vertical(g6)
    c: DistanceY(g6,g6) = 1.8
    c: Coincident(g7,g6)
    c: Vertical(g7)
    c: DistanceY(g7,g7) = 2
    c: Coincident(g8,g7)
    c: Horizontal(g8)
    c: DistanceX(g8,g8) = 125
    c: Coincident(g9,g7)
    c: Horizontal(g9)
    c: DistanceX(g9,g9) = 125
    c: Coincident(g10,g3)
    c: Coincident(g10,g5)
    c: Coincident(g11,g8)
    c: Coincident(g11,g9)
FEATURE [PartDesign::Pad] Pad003
  BaseFeature = -> Chamfer001
  Direction = (1,1,1)
  Length = 2.5
  Length2 = 100
  Profile = -> Sketch010
  Type = 0
FEATURE [PartDesign::Chamfer] Chamfer002
  Angle = 45
  Base = -> Chamfer001 [Edge396,Edge384,Edge381,Edge370,Edge467,Edge454,Edge448,Edge442,Edge727,Edge714,Edge708,Edge702]
  BaseFeature = -> Chamfer001
  ChamferType = 0
  FlipDirection = false
  Size = 0.99
  Size2 = 1
  SupportTransform = false
FEATURE [Sketcher::SketchObject] Sketch012
  FullyConstrained = true
  MapMode = 5
  Placement = pos=(0,0,0) rot=(1,0,0;3.14159rad)
  Support = -> [Chamfer002]
  sketch-geometry (12):
    g0: LineSegment StartX=0 StartY=0 StartZ=0 EndX=150 EndY=0 EndZ=0
    g1: LineSegment StartX=150 StartY=0 StartZ=0 EndX=150 EndY=-22 EndZ=0
    g2: LineSegment StartX=150 StartY=-22 StartZ=0 EndX=142 EndY=-22 EndZ=0
    g3: LineSegment StartX=142 StartY=-22 StartZ=0 EndX=142 EndY=-24 EndZ=0
    g4: LineSegment StartX=142 StartY=-22 StartZ=0 EndX=17 EndY=-22 EndZ=0
    g5: LineSegment StartX=142 StartY=-24 StartZ=0 EndX=17 EndY=-24 EndZ=0
    g6: LineSegment StartX=142 StartY=-24 StartZ=0 EndX=142 EndY=-25.8 EndZ=0
    g7: LineSegment StartX=142 StartY=-25.8 StartZ=0 EndX=142 EndY=-27.8 EndZ=0
    g8: LineSegment StartX=142 StartY=-25.8 StartZ=0 EndX=17 EndY=-25.8 EndZ=0
    g9: LineSegment StartX=142 StartY=-27.8 StartZ=0 EndX=17 EndY=-27.8 EndZ=0
    g10: LineSegment StartX=17 StartY=-24 StartZ=0 EndX=17 EndY=-22 EndZ=0
    g11: LineSegment StartX=17 StartY=-27.8 StartZ=0 EndX=17 EndY=-25.8 EndZ=0
  constraints (34):
    c: Coincident(g0,g-1)
    c: Horizontal(g0)
    c: DistanceX(g0,g0) = 150
    c: Coincident(g1,g0)
    c: Vertical(g1)
    c: DistanceY(g1,g1) = 22
    c: Coincident(g2,g1)
    c: Horizontal(g2)
    c: DistanceX(g2,g2) = 8
    c: Coincident(g3,g2)
    c: Vertical(g3)
    c: DistanceY(g3,g3) = 2
    c: Coincident(g4,g3)
    c: Horizontal(g4)
    c: DistanceX(g4,g4) = 125
    c: Coincident(g5,g3)
    c: Horizontal(g5)
    c: DistanceX(g5,g5) = 125
    c: Coincident(g6,g3)
    c: Vertical(g6)
    c: DistanceY(g6,g6) = 1.8
    c: Coincident(g7,g6)
    c: Vertical(g7)
    c: DistanceY(g7,g7) = 2
    c: Coincident(g8,g7)
    c: Horizontal(g8)
    c: DistanceX(g8,g8) = 125
    c: Coincident(g9,g7)
    c: Horizontal(g9)
    c: DistanceX(g9,g9) = 125
    c: Coincident(g10,g5)
    c: Coincident(g10,g4)
    c: Coincident(g11,g9)
    c: Coincident(g11,g8)
FEATURE [PartDesign::Pad] Pad004
  BaseFeature = -> Chamfer002
  Direction = (1,1,1)
  Length = 1.5
  Length2 = 100
  Profile = -> Sketch012
  Type = 0
FEATURE [Sketcher::SketchObject] Sketch013
  FullyConstrained = true
  MapMode = 5
  Placement = pos=(0,0,-2.5) rot=(1,0,0;3.14159rad)
  Support = -> [Pad003]
  sketch-geometry (42):
    g0: LineSegment StartX=0 StartY=0 StartZ=0 EndX=150 EndY=0 EndZ=0
    g1: LineSegment StartX=150 StartY=0 StartZ=0 EndX=150 EndY=-27.8 EndZ=0
    g2: LineSegment StartX=150 StartY=-27.8 StartZ=0 EndX=139.4 EndY=-27.8 EndZ=0
    g3: LineSegment StartX=139.4 StartY=-27.8 StartZ=0 EndX=137.7 EndY=-27.8 EndZ=0
    g4: LineSegment StartX=137.7 StartY=-27.8 StartZ=0 EndX=137.7 EndY=-25.8 EndZ=0
    g5: LineSegment StartX=137.7 StartY=-25.8 StartZ=0 EndX=139.4 EndY=-25.8 EndZ=0
    g6: LineSegment StartX=139.4 StartY=-25.8 StartZ=0 EndX=139.4 EndY=-27.8 EndZ=0
    g7: LineSegment StartX=137.7 StartY=-27.8 StartZ=0 EndX=127.8 EndY=-27.8 EndZ=0
    g8: LineSegment StartX=127.8 StartY=-27.8 StartZ=0 EndX=126.1 EndY=-27.8 EndZ=0
    g9: LineSegment StartX=126.1 StartY=-27.8 StartZ=0 EndX=126.1 EndY=-25.8 EndZ=0
    g10: LineSegment StartX=126.1 StartY=-25.8 StartZ=0 EndX=127.8 EndY=-25.8 EndZ=0
    g11: LineSegment StartX=127.8 StartY=-25.8 StartZ=0 EndX=127.8 EndY=-27.8 EndZ=0
    g12: LineSegment StartX=126.1 StartY=-27.8 StartZ=0 EndX=104.2 EndY=-27.8 EndZ=0
    g13: LineSegment StartX=104.2 StartY=-27.8 StartZ=0 EndX=102.5 EndY=-27.8 EndZ=0
    g14: LineSegment StartX=102.5 StartY=-27.8 StartZ=0 EndX=102.5 EndY=-25.8 EndZ=0
    g15: LineSegment StartX=102.5 StartY=-25.8 StartZ=0 EndX=104.2 EndY=-25.8 EndZ=0
    g16: LineSegment StartX=104.2 StartY=-25.8 StartZ=0 EndX=104.2 EndY=-27.8 EndZ=0
    g17: LineSegment StartX=102.5 StartY=-27.8 StartZ=0 EndX=92.6 EndY=-27.8 EndZ=0
    g18: LineSegment StartX=92.6 StartY=-27.8 StartZ=0 EndX=90.9 EndY=-27.8 EndZ=0
    g19: LineSegment StartX=90.9 StartY=-27.8 StartZ=0 EndX=90.9 EndY=-25.8 EndZ=0
    g20: LineSegment StartX=90.9 StartY=-25.8 StartZ=0 EndX=92.6 EndY=-25.8 EndZ=0
    g21: LineSegment StartX=92.6 StartY=-25.8 StartZ=0 EndX=92.6 EndY=-27.8 EndZ=0
    g22: LineSegment StartX=90.9 StartY=-27.8 StartZ=0 EndX=69 EndY=-27.8 EndZ=0
    g23: LineSegment StartX=69 StartY=-27.8 StartZ=0 EndX=67.3 EndY=-27.8 EndZ=0
    g24: LineSegment StartX=67.3 StartY=-27.8 StartZ=0 EndX=67.3 EndY=-25.8 EndZ=0
    g25: LineSegment StartX=67.3 StartY=-25.8 StartZ=0 EndX=69 EndY=-25.8 EndZ=0
    g26: LineSegment StartX=69 StartY=-25.8 StartZ=0 EndX=69 EndY=-27.8 EndZ=0
    g27: LineSegment StartX=67.3 StartY=-27.8 StartZ=0 EndX=57.4 EndY=-27.8 EndZ=0
    g28: LineSegment StartX=57.4 StartY=-27.8 StartZ=0 EndX=55.7 EndY=-27.8 EndZ=0
    g29: LineSegment StartX=55.7 StartY=-27.8 StartZ=0 EndX=55.7 EndY=-25.8 EndZ=0
    g30: LineSegment StartX=55.7 StartY=-25.8 StartZ=0 EndX=57.4 EndY=-25.8 EndZ=0
    g31: LineSegment StartX=57.4 StartY=-25.8 StartZ=0 EndX=57.4 EndY=-27.8 EndZ=0
    g32: LineSegment StartX=55.7 StartY=-27.8 StartZ=0 EndX=33.8 EndY=-27.8 EndZ=0
    g33: LineSegment StartX=33.8 StartY=-27.8 StartZ=0 EndX=32.1 EndY=-27.8 EndZ=0
    g34: LineSegment StartX=32.1 StartY=-27.8 StartZ=0 EndX=32.1 EndY=-25.8 EndZ=0
    g35: LineSegment StartX=32.1 StartY=-25.8 StartZ=0 EndX=33.8 EndY=-25.8 EndZ=0
    g36: LineSegment StartX=33.8 StartY=-25.8 StartZ=0 EndX=33.8 EndY=-27.8 EndZ=0
    g37: LineSegment StartX=32.1 StartY=-27.8 StartZ=0 EndX=22.2 EndY=-27.8 EndZ=0
    g38: LineSegment StartX=22.2 StartY=-27.8 StartZ=0 EndX=20.5 EndY=-27.8 EndZ=0
    g39: LineSegment StartX=20.5 StartY=-27.8 StartZ=0 EndX=20.5 EndY=-25.8 EndZ=0
    g40: LineSegment StartX=20.5 StartY=-25.8 StartZ=0 EndX=22.2 EndY=-25.8 EndZ=0
    g41: LineSegment StartX=22.2 StartY=-25.8 StartZ=0 EndX=22.2 EndY=-27.8 EndZ=0
  constraints (118):
    c: Coincident(g0,g-1)
    c: Horizontal(g0)
    c: DistanceX(g0,g0) = 150
    c: Coincident(g1,g0)
    c: Vertical(g1)
    c: DistanceY(g1,g1) = 27.8
    c: Coincident(g2,g1)
    c: Horizontal(g2)
    c: DistanceX(g2,g2) = 10.6
    c: Coincident(g3,g4)
    c: Coincident(g4,g5)
    c: Coincident(g5,g6)
    c: Coincident(g6,g3)
    c: Horizontal(g3)
    c: Horizontal(g5)
    c: Vertical(g4)
    c: Vertical(g6)
    c: Coincident(g3,g2)
    c: DistanceX(g3,g3) = 1.7
    c: DistanceY(g4,g4) = 2
    c: Coincident(g7,g3)
    c: Horizontal(g7)
    c: DistanceX(g7,g7) = 9.9
    c: Coincident(g8,g9)
    c: Coincident(g9,g10)
    c: Coincident(g10,g11)
    c: Coincident(g11,g8)
    c: Horizontal(g8)
    c: Horizontal(g10)
    c: Vertical(g9)
    c: Vertical(g11)
    c: Coincident(g8,g7)
    c: DistanceX(g10,g10) = 1.7
    c: DistanceY(g9,g9) = 2
    c: Coincident(g12,g8)
    c: Horizontal(g12)
    c: DistanceX(g12,g12) = 21.9
    c: Coincident(g13,g14)
    c: Coincident(g14,g15)
    c: Coincident(g15,g16)
    c: Coincident(g16,g13)
    c: Horizontal(g13)
    c: Horizontal(g15)
    c: Vertical(g14)
    c: Vertical(g16)
    c: Coincident(g13,g12)
    c: DistanceX(g15,g15) = 1.7
    c: DistanceY(g14,g14) = 2
    c: Coincident(g17,g13)
    c: Horizontal(g17)
    c: DistanceX(g17,g17) = 9.9
    c: Coincident(g18,g19)
    c: Coincident(g19,g20)
    c: Coincident(g20,g21)
    c: Coincident(g21,g18)
    c: Horizontal(g18)
    c: Horizontal(g20)
    c: Vertical(g19)
    c: Vertical(g21)
    c: Coincident(g18,g17)
    c: DistanceX(g18,g18) = 1.7
    c: DistanceY(g19,g19) = 2
    c: Coincident(g22,g18)
    c: Horizontal(g22)
    c: DistanceX(g22,g22) = 21.9
    c: Coincident(g23,g24)
    c: Coincident(g24,g25)
    c: Coincident(g25,g26)
    c: Coincident(g26,g23)
    c: Horizontal(g23)
    c: Horizontal(g25)
    c: Vertical(g24)
    c: Vertical(g26)
    c: Coincident(g23,g22)
    c: DistanceX(g25,g25) = 1.7
    c: DistanceY(g24,g24) = 2
    c: Coincident(g27,g23)
    c: Horizontal(g27)
    c: DistanceX(g27,g27) = 9.9
    c: Coincident(g28,g29)
    c: Coincident(g29,g30)
    c: Coincident(g30,g31)
    c: Coincident(g31,g28)
    c: Horizontal(g28)
    c: Horizontal(g30)
    c: Vertical(g29)
    c: Vertical(g31)
    c: Coincident(g28,g27)
    c: DistanceX(g28,g28) = 1.7
    c: DistanceY(g29,g29) = 2
    c: Coincident(g32,g28)
    c: Horizontal(g32)
    c: DistanceX(g32,g32) = 21.9
    c: Coincident(g33,g34)
    c: Coincident(g34,g35)
    c: Coincident(g35,g36)
    c: Coincident(g36,g33)
    c: Horizontal(g33)
    c: Horizontal(g35)
    c: Vertical(g34)
    c: Vertical(g36)
    c: Coincident(g33,g32)
    c: DistanceX(g35,g35) = 1.7
    c: DistanceY(g34,g34) = 2
    c: Coincident(g37,g33)
    c: Horizontal(g37)
    c: DistanceX(g37,g37) = 9.9
    c: Coincident(g38,g39)
    c: Coincident(g39,g40)
    c: Coincident(g40,g41)
    c: Coincident(g41,g38)
    c: Horizontal(g38)
    c: Horizontal(g40)
    c: Vertical(g39)
    c: Vertical(g41)
    c: Coincident(g38,g37)
    c: DistanceX(g38,g38) = 1.7
    c: DistanceY(g39,g39) = 2
FEATURE [PartDesign::Pocket] Pocket005
  BaseFeature = -> Pad004
  Length = 2.5
  Length2 = 100
  Profile = -> Sketch013
  Type = 0
FEATURE [Sketcher::SketchObject] Sketch014
  FullyConstrained = true
  MapMode = 5
  Placement = pos=(0,0,0) rot=(1,0,0;3.14159rad)
  Support = -> [Pocket005]
  sketch-geometry (12):
    g0: LineSegment StartX=0 StartY=0 StartZ=0 EndX=150 EndY=0 EndZ=0
    g1: LineSegment StartX=150 StartY=0 StartZ=0 EndX=150 EndY=-20 EndZ=0
    g2: LineSegment StartX=150 StartY=-20 StartZ=0 EndX=142 EndY=-20 EndZ=0
    g3: LineSegment StartX=142 StartY=-20 StartZ=0 EndX=42 EndY=-20 EndZ=0
    g4: LineSegment StartX=42 StartY=-20 StartZ=0 EndX=42 EndY=-17.5 EndZ=0
    g5: LineSegment StartX=42 StartY=-17.5 StartZ=0 EndX=142 EndY=-17.5 EndZ=0
    g6: LineSegment StartX=142 StartY=-17.5 StartZ=0 EndX=142 EndY=-20 EndZ=0
    g7: LineSegment StartX=142 StartY=-17.5 StartZ=0 EndX=142 EndY=-11.5 EndZ=0
    g8: LineSegment StartX=142 StartY=-11.5 StartZ=0 EndX=27 EndY=-11.5 EndZ=0
    g9: LineSegment StartX=27 StartY=-11.5 StartZ=0 EndX=27 EndY=-9 EndZ=0
    g10: LineSegment StartX=27 StartY=-9 StartZ=0 EndX=142 EndY=-9 EndZ=0
    g11: LineSegment StartX=142 StartY=-9 StartZ=0 EndX=142 EndY=-11.5 EndZ=0
  constraints (34):
    c: Coincident(g0,g-1)
    c: Horizontal(g0)
    c: DistanceX(g0,g0) = 150
    c: Coincident(g1,g0)
    c: Vertical(g1)
    c: DistanceY(g1,g1) = 20
    c: Coincident(g2,g1)
    c: Horizontal(g2)
    c: DistanceX(g2,g2) = 8
    c: Coincident(g3,g4)
    c: Coincident(g4,g5)
    c: Coincident(g5,g6)
    c: Coincident(g6,g3)
    c: Horizontal(g3)
    c: Horizontal(g5)
    c: Vertical(g4)
    c: Vertical(g6)
    c: Coincident(g3,g2)
    c: DistanceX(g5,g5) = 100
    c: DistanceY(g4,g4) = 2.5
    c: Coincident(g7,g5)
    c: Vertical(g7)
    c: DistanceY(g7,g7) = 6
    c: Coincident(g8,g9)
    c: Coincident(g9,g10)
    c: Coincident(g10,g11)
    c: Coincident(g11,g8)
    c: Horizontal(g8)
    c: Horizontal(g10)
    c: Vertical(g9)
    c: Vertical(g11)
    c: Coincident(g8,g7)
    c: DistanceX(g10,g10) = 115
    c: DistanceY(g11,g11) = 2.5
FEATURE [PartDesign::Pad] Pad005
  BaseFeature = -> Pocket005
  Direction = (1,1,1)
  Length = 4
  Length2 = 100
  Profile = -> Sketch014
  Type = 0
FEATURE [Sketcher::SketchObject] Sketch015
  FullyConstrained = true
  MapMode = 5
  Placement = pos=(0,0,-1.5) rot=(1,0,0;3.14159rad)
  Support = -> [Pad005]
  sketch-geometry (7):
    g0: LineSegment StartX=0 StartY=0 StartZ=0 EndX=150 EndY=0 EndZ=0
    g1: LineSegment StartX=150 StartY=0 StartZ=0 EndX=150 EndY=-24 EndZ=0
    g2: LineSegment StartX=150 StartY=-24 StartZ=0 EndX=42 EndY=-24 EndZ=0
    g3: LineSegment StartX=42 StartY=-24 StartZ=0 EndX=34 EndY=-24 EndZ=0
    g4: LineSegment StartX=34 StartY=-24 StartZ=0 EndX=34 EndY=-22 EndZ=0
    g5: LineSegment StartX=34 StartY=-22 StartZ=0 EndX=42 EndY=-22 EndZ=0
    g6: LineSegment StartX=42 StartY=-22 StartZ=0 EndX=42 EndY=-24 EndZ=0
  constraints (20):
    c: Coincident(g0,g-1)
    c: Horizontal(g0)
    c: DistanceX(g0,g0) = 150
    c: Coincident(g1,g0)
    c: Vertical(g1)
    c: DistanceY(g1,g1) = 24
    c: Coincident(g2,g1)
    c: Horizontal(g2)
    c: DistanceX(g2,g2) = 108
    c: Coincident(g3,g4)
    c: Coincident(g4,g5)
    c: Coincident(g5,g6)
    c: Coincident(g6,g3)
    c: Horizontal(g3)
    c: Horizontal(g5)
    c: Vertical(g4)
    c: Vertical(g6)
    c: Coincident(g3,g2)
    c: DistanceX(g5,g5) = 8
    c: DistanceY(g4,g4) = 2
FEATURE [PartDesign::Pocket] Pocket006
  BaseFeature = -> Pad005
  Length = 1.5
  Length2 = 100
  Profile = -> Sketch015
  Type = 0
FEATURE [PartDesign::Chamfer] Chamfer003
  Angle = 45
  Base = -> Pocket006 [Edge505,Edge497,Edge489,Edge481,Edge473,Edge465,Edge457,Edge449,Edge442,Edge422,Edge426]
  BaseFeature = -> Pocket006
  ChamferType = 0
  FlipDirection = false
  Size = 1.45
  Size2 = 1
  SupportTransform = false
FEATURE [PartDesign::Chamfer] Chamfer004
  Angle = 45
  Base = -> Chamfer003 [Edge600,Edge604]
  BaseFeature = -> Chamfer003
  ChamferType = 0
  FlipDirection = false
  Size = 2.49
  Size2 = 1
  SupportTransform = false
FEATURE [Sketcher::SketchObject] Sketch016
  FullyConstrained = true
  MapMode = 5
  Placement = pos=(4.5,0,0) rot=(0.57735,0.57735,0.57735;2.0944rad)
  Support = -> [Chamfer004]
  sketch-geometry (7):
    g0: LineSegment StartX=0 StartY=0 StartZ=0 EndX=150 EndY=0 EndZ=0
    g1: LineSegment StartX=150 StartY=0 StartZ=0 EndX=150 EndY=-8 EndZ=0
    g2: LineSegment StartX=150 StartY=-8 StartZ=0 EndX=72 EndY=-8 EndZ=0
    g3: LineSegment StartX=72 StartY=-8 StartZ=0 EndX=21.7 EndY=-8 EndZ=0
    g4: LineSegment StartX=21.7 StartY=-8 StartZ=0 EndX=21.7 EndY=-13 EndZ=0
    g5: LineSegment StartX=21.7 StartY=-13 StartZ=0 EndX=72 EndY=-13 EndZ=0
    g6: LineSegment StartX=72 StartY=-13 StartZ=0 EndX=72 EndY=-8 EndZ=0
  constraints (20):
    c: Coincident(g0,g-1)
    c: Horizontal(g0)
    c: DistanceX(g0,g0) = 150
    c: Coincident(g1,g0)
    c: Vertical(g1)
    c: DistanceY(g1,g1) = 8
    c: Coincident(g2,g1)
    c: Horizontal(g2)
    c: DistanceX(g2,g2) = 78
    c: Coincident(g3,g4)
    c: Coincident(g4,g5)
    c: Coincident(g5,g6)
    c: Coincident(g6,g3)
    c: Horizontal(g3)
    c: Horizontal(g5)
    c: Vertical(g4)
    c: Vertical(g6)
    c: Coincident(g3,g2)
    c: DistanceX(g3,g3) = 50.3
    c: DistanceY(g6,g6) = 5
FEATURE [PartDesign::Pad] Pad006
  BaseFeature = -> Chamfer004
  Direction = (1,1,1)
  Length = 5
  Length2 = 100
  Profile = -> Sketch016
  Type = 0
FEATURE [Sketcher::SketchObject] Sketch020
  FullyConstrained = true
  MapMode = 5
  Placement = pos=(0,0,-13) rot=(1,0,0;3.14159rad)
  Support = -> [Pad006]
  sketch-geometry (14):
    g0: LineSegment StartX=0 StartY=0 StartZ=0 EndX=0 EndY=-21.7 EndZ=0
    g1: LineSegment StartX=0 StartY=-21.7 StartZ=0 EndX=6.1 EndY=-21.7 EndZ=0
    g2: LineSegment StartX=6.1 StartY=-21.7 StartZ=0 EndX=7.9 EndY=-21.7 EndZ=0
    g3: LineSegment StartX=7.9 StartY=-21.7 StartZ=0 EndX=7.9 EndY=-72 EndZ=0
    g4: LineSegment StartX=7.9 StartY=-72 StartZ=0 EndX=6.1 EndY=-72 EndZ=0
    g5: LineSegment StartX=6.1 StartY=-72 StartZ=0 EndX=6.1 EndY=-21.7 EndZ=0
    g6: LineSegment StartX=7.9 StartY=-21.7 StartZ=0 EndX=9.5 EndY=-21.7 EndZ=0
    g7: LineSegment StartX=9.5 StartY=-21.7 StartZ=0 EndX=9.5 EndY=-72 EndZ=0
    g8: LineSegment StartX=9.5 StartY=-72 StartZ=0 EndX=7.9 EndY=-72 EndZ=0
    g9: LineSegment StartX=7.9 StartY=-72 StartZ=0 EndX=7.9 EndY=-21.7 EndZ=0
    g10: LineSegment StartX=6.1 StartY=-72 StartZ=0 EndX=4.5 EndY=-72 EndZ=0
    g11: LineSegment StartX=4.5 StartY=-72 StartZ=0 EndX=4.5 EndY=-21.7 EndZ=0
    g12: LineSegment StartX=4.5 StartY=-21.7 StartZ=0 EndX=6.1 EndY=-21.7 EndZ=0
    g13: LineSegment StartX=6.1 StartY=-21.7 StartZ=0 EndX=6.1 EndY=-72 EndZ=0
  constraints (37):
    c: Coincident(g0,g-1)
    c: PointOnObject(g0,g-2)
    c: DistanceY(g0,g0) = 21.7
    c: Coincident(g1,g0)
    c: Horizontal(g1)
    c: DistanceX(g1,g1) = 6.1
    c: Coincident(g2,g3)
    c: Coincident(g3,g4)
    c: Coincident(g4,g5)
    c: Coincident(g5,g2)
    c: Horizontal(g2)
    c: Horizontal(g4)
    c: Vertical(g3)
    c: Vertical(g5)
    c: Coincident(g2,g1)
    c: DistanceY(g5,g5) = 50.3
    c: DistanceX(g2,g2) = 1.8
    c: Coincident(g6,g7)
    c: Coincident(g7,g8)
    c: Coincident(g8,g9)
    c: Coincident(g9,g6)
    c: Horizontal(g6)
    c: Horizontal(g8)
    c: Vertical(g7)
    c: Coincident(g6,g2)
    c: Coincident(g3,g8)
    c: DistanceX(g8,g8) = 1.6
    c: Coincident(g10,g11)
    c: Coincident(g11,g12)
    c: Coincident(g12,g13)
    c: Coincident(g13,g10)
    c: Horizontal(g10)
    c: Horizontal(g12)
    c: Vertical(g11)
    c: Coincident(g10,g4)
    c: Coincident(g12,g1)
    c: DistanceX(g12,g12) = 1.6
FEATURE [PartDesign::Body] Body
  Group = -> [Sketch,Pad,Sketch001,Pocket,LinearPattern,Sketch002,Pocket001,LinearPattern001,Sketch003,Pad001,Sketch004,Hole,LinearPattern003,Chamfer,Sketch005,Pocket002,Sketch006,Pocket003,Sketch008,Pocket004,Sketch009,Pad002,LinearPattern004,Chamfer001,Sketch010,Pad003,Chamfer002,Sketch012,Pad004,Sketch013,Pocket005,Sketch014,Pad005,Sketch015,Pocket006,Chamfer003,Chamfer004,Sketch016,Pad006,Sketch018,+6 more]
  Origin = -> Origin
  Tip = -> Chamfer005
FEATURE [Sketcher::SketchObject] Sketch018
  FullyConstrained = true
  MapMode = 5
  Placement = pos=(4.5,0,0) rot=(0.57735,0.57735,0.57735;2.0944rad)
  Support = -> [Chamfer005]
  sketch-geometry (6):
    g0: LineSegment StartX=0 StartY=0 StartZ=0 EndX=0 EndY=-25 EndZ=0
    g1: LineSegment StartX=0 StartY=-25 StartZ=0 EndX=80 EndY=-25 EndZ=0
    g2: LineSegment StartX=80 StartY=-25 StartZ=0 EndX=106.4 EndY=-25 EndZ=0
    g3: LineSegment StartX=106.4 StartY=-25 StartZ=0 EndX=106.4 EndY=-22.3 EndZ=0
    g4: LineSegment StartX=106.4 StartY=-22.3 StartZ=0 EndX=80 EndY=-22.3 EndZ=0
    g5: LineSegment StartX=80 StartY=-22.3 StartZ=0 EndX=80 EndY=-25 EndZ=0
  constraints (17):
    c: Coincident(g0,g-1)
    c: PointOnObject(g0,g-2)
    c: DistanceY(g0,g0) = 25
    c: Coincident(g1,g0)
    c: Horizontal(g1)
    c: DistanceX(g1,g1) = 80
    c: Coincident(g2,g3)
    c: Coincident(g3,g4)
    c: Coincident(g4,g5)
    c: Coincident(g5,g2)
    c: Horizontal(g2)
    c: Horizontal(g4)
    c: Vertical(g3)
    c: Vertical(g5)
    c: Coincident(g2,g1)
    c: DistanceX(g4,g4) = 26.4
    c: DistanceY(g3,g3) = 2.7
FEATURE [PartDesign::Pocket] Pocket008
  BaseFeature = -> Pad006
  Length = 4.5
  Length2 = 100
  Profile = -> Sketch018
  Type = 0
FEATURE [Sketcher::SketchObject] Sketch019
  FullyConstrained = true
  MapMode = 5
  Placement = pos=(4.5,0,0) rot=(0.57735,0.57735,0.57735;2.0944rad)
  Support = -> [Pocket008]
  sketch-geometry (6):
    g0: LineSegment StartX=0 StartY=0 StartZ=0 EndX=0 EndY=-10 EndZ=0
    g1: LineSegment StartX=0 StartY=-10 StartZ=0 EndX=115 EndY=-10 EndZ=0
    g2: LineSegment StartX=115 StartY=-10 StartZ=0 EndX=125.1 EndY=-10 EndZ=0
    g3: LineSegment StartX=125.1 StartY=-10 StartZ=0 EndX=125.1 EndY=-31 EndZ=0
    g4: LineSegment StartX=125.1 StartY=-31 StartZ=0 EndX=115 EndY=-31 EndZ=0
    g5: LineSegment StartX=115 StartY=-31 StartZ=0 EndX=115 EndY=-10 EndZ=0
  constraints (17):
    c: Coincident(g0,g-1)
    c: PointOnObject(g0,g-2)
    c: DistanceY(g0,g0) = 10
    c: Coincident(g1,g0)
    c: Horizontal(g1)
    c: DistanceX(g1,g1) = 115
    c: Coincident(g2,g3)
    c: Coincident(g3,g4)
    c: Coincident(g4,g5)
    c: Coincident(g5,g2)
    c: Horizontal(g2)
    c: Horizontal(g4)
    c: Vertical(g3)
    c: Vertical(g5)
    c: Coincident(g2,g1)
    c: DistanceX(g2,g2) = 10.1
    c: DistanceY(g3,g3) = 21
FEATURE [PartDesign::Pocket] Pocket009
  BaseFeature = -> Pocket008
  Length = 4.5
  Length2 = 100
  Profile = -> Sketch019
  Type = 0
FEATURE [PartDesign::Pad] Pad007
  BaseFeature = -> Pocket009
  Direction = (1,1,1)
  Length = 2
  Length2 = 100
  Profile = -> Sketch020
  Type = 0
FEATURE [PartDesign::Chamfer] Chamfer005
  Angle = 45
  Base = -> Pad007 [Edge1129]
  BaseFeature = -> Pad007
  ChamferType = 2
  FlipDirection = false
  Size = 4.99
  Size2 = 1
  SupportTransform = false
